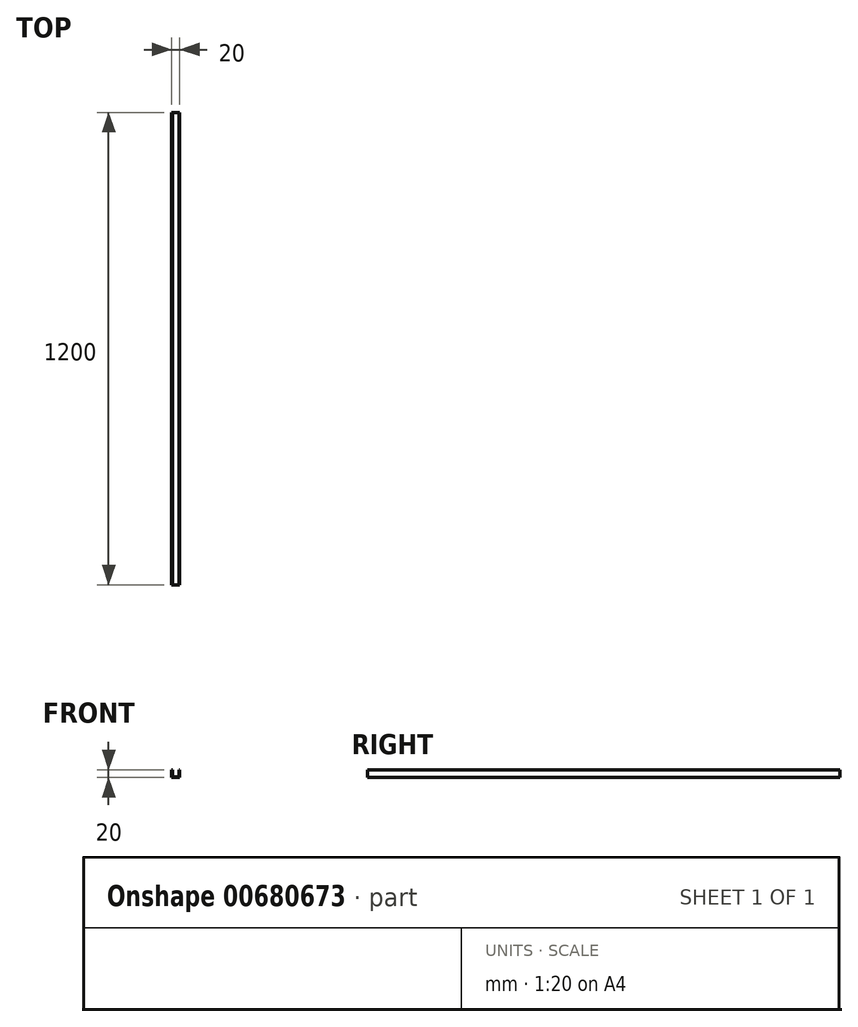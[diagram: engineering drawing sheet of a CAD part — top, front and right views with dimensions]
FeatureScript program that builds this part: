
annotation { "Feature Type Name" : "Feature", "Feature Type Description" : "" }
export const myFeature = defineFeature(function(context is Context, id is Id, definition is map)
    precondition{}
    {
        {
            var Q0;
            Q0=qCreatedBy(makeId("Front.planeOp"),FACE);
            var sketch = newSketch(context, id + "F0", { "sketchPlane" : qUnion([Q0])});
            skLineSegment(sketch, "E0", {"start": v(0, 0) * mm, "end": v(20, 0) * mm});
            skLineSegment(sketch, "E1", {"start": v(20, 0) * mm, "end": v(20, 20) * mm});
            skLineSegment(sketch, "E2", {"start": v(0, 0) * mm, "end": v(0, 20) * mm});
            skLineSegment(sketch, "E3.0", {"start": v(1.5, 1.5) * mm, "end": v(1.5, 20) * mm});
            skLineSegment(sketch, "E3.1", {"start": v(1.5, 1.5) * mm, "end": v(18.5, 1.5) * mm});
            skLineSegment(sketch, "E3.2", {"start": v(18.5, 1.5) * mm, "end": v(18.5, 20) * mm});
            skLineSegment(sketch, "E4", {"start": v(1.5, 20) * mm, "end": v(0, 20) * mm});
            skLineSegment(sketch, "E5", {"start": v(18.5, 20) * mm, "end": v(20, 20) * mm});
            skSolve(sketch);
        }
        {
            var Q0;
            Q0=makeQuery(id+"F0.imprint","IMPRINT",FACE,{"disambiguationData":[TD([[makeQuery(id+"F0.imprint","IMPRINT",EDGE,{"derivedFrom":sQuery(id+"F0.wireOp",EDGE,"E0")}),1.0]])]});
            extrude(context, id + "F1", {"entities" : qUnion([Q0]), "endBound" : BoundingType.SYMMETRIC, "depth" : 1200 * mm, "offsetDistance" : 25 * mm});
        }
    });
